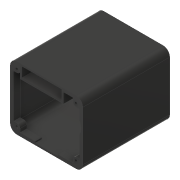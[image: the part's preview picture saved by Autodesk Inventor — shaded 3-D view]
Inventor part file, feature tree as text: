
AUTODESK INVENTOR PART (.ipt)
format: ipt  version: 2017 (Build 210142000, 142)  size: 1,119,232 bytes
history: native  units: in
note: dims shown in document units (in); Inventor stores cm internally (conversion verified against a paired STEP export)
features: sketch x38, extrude x36, projected_geometry x25, reference x20, other x11, fillet x4, chamfer x3, plane x3
ambient origin geometry x8: Origin, YZ Plane, XZ Plane, XY Plane, X Axis, Y Axis, Z Axis, Center Point
bodies: Solid1 (feature_tree)
feature tree (140):
  extrude  "Extrusion1"  Depth=3.25in
  extrude  "Extrusion2"  Depth=0.125in TaperAngle=0.0deg
  extrude  "Extrusion3"  Depth=0.125in
  chamfer  "Chamfer1"  Distance=0.125in
  sketch  "Sketch4"  dims[d8=0.125in]
  plane  "Work Plane1"
  extrude  "Extrusion4"  Depth=0.25in
  chamfer  "Chamfer2"  Distance=0.25in
  extrude  "Extrusion5"  Depth=0.1in
  extrude  "Extrusion6"  Depth=0.1in
  extrude  "Extrusion7"  Depth=0.1in
  fillet  "Fillet1"  Radius=0.275in
  extrude  "Extrusion8"  Depth=0.0625in TaperAngle=0.0deg
  fillet  "Fillet2"  Radius=0.0625in
  fillet  "Fillet3"  Radius=0.0625in
  extrude  "Extrusion9"  Depth=0.05in
  extrude  "Extrusion10"  Depth=0.05in
  fillet  "Fillet4"  Radius=2.5in
  sketch  "Sketch13"  dims[d30=0.175in d31=0.0in d32=1.0in d33=0.0in d34=0.0625in d35=0.0625in]
  plane  "Work Plane2"
  extrude  "Extrusion11"  Depth=0.125in TaperAngle=0.0deg
  sketch  "Sketch14"  dims[d36=0.0625in d37=0.05in]
  plane  "Work Plane3"
  extrude  "Extrusion12"  Depth=0.05in
  extrude  "Extrusion13"  Depth=0.25in
  extrude  "Extrusion14"  Depth=0.05in
  extrude  "Extrusion16"  Depth=0.05in
  extrude  "Extrusion17"  [1 undecoded]
  extrude  "Extrusion18"  Depth=0.0625in TaperAngle=0.0deg
  extrude  "Extrusion19"  Depth=0.5in TaperAngle=0.0deg
  sketch  "Sketch24"  dims[d58=0.25in d59=0.0in d60=0.0625in d61=0.0in]
  extrude  "Extrusion20"  Depth=0.01in
  extrude  "Extrusion21"  TaperAngle=0.0deg  [1 undecoded]
  extrude  "Extrusion22"  Depth=1.0in TaperAngle=0.0deg
  extrude  "Extrusion23"  Depth=0.85in
  extrude  "Extrusion24"  Depth=0.0625in
  extrude  "Extrusion25"  Depth=0.375in
  extrude  "Extrusion26"  Depth=0.1in
  extrude  "Extrusion27"  Depth=0.25in TaperAngle=0.0deg
  extrude  "Extrusion28"  Depth=0.0625in
  extrude  "Extrusion29"  Depth=0.25in TaperAngle=0.0deg
  extrude  "Extrusion30"  Depth=0.1in
  extrude  "Extrusion31"  Depth=0.1in TaperAngle=0.0deg
  extrude  "Extrusion32"  Depth=0.1in TaperAngle=0.0deg
  extrude  "Extrusion33"  Depth=0.375in
  extrude  "Extrusion34"  Depth=0.125in TaperAngle=45.0deg
  chamfer  "Chamfer3"  Distance=0.1in
  extrude  "Extrusion35"  Depth=0.1in TaperAngle=0.0deg
  extrude  "Extrusion36"  [1 undecoded]
  extrude  "Extrusion37"  [1 undecoded]
  sketch  "Sketch1"  dims[d0=3.25in d1=0.0in d2=0.015in]
  reference  "Reference1"
  sketch  "Sketch2"  dims[d3=0.015in d4=0.125in d5=0.0in]
  reference  "Reference2"
  reference  "Reference3"
  reference  "Reference4"
  reference  "Reference5"
  reference  "Reference6"
  sketch  "Sketch3"  dims[d6=0.125in d7=0.125in]
  projected_geometry  "Projected Loop1"
  projected_geometry  "Projected Loop2"
  reference  "Reference7"
  reference  "Reference8"
  reference  "Reference9"
  reference  "Reference10"
  reference  "Reference11"
  sketch  "Sketch5"  dims[d9=0.125in d10=0.125in d11=0.0in]
  reference  "Reference12"
  reference  "Reference13"
  sketch  "Sketch6"  dims[d12=0.057in d13=0.125in d14=45.0deg d15=0.25in]
  sketch  "Sketch8"  dims[d16=0.1in]
  projected_geometry  "Projected Loop3"
  sketch  "Sketch9"  dims[d17=0.1in d19=0.25in d20=0.0in]
  reference  "Reference14"
  reference  "Reference15"
  sketch  "Sketch10"  dims[d21=0.075in d22=0.125in d23=45.0deg d24=0.1in]
  projected_geometry  "Projected Loop4"
  projected_geometry  "Projected Loop5"
  sketch  "Sketch11"  dims[d25=0.5in d26=0.1in]
  projected_geometry  "Projected Loop6"
  sketch  "Sketch12"  dims[d27=0.1in d28=0.275in d29=0.275in]
  projected_geometry  "Projected Loop7"
  projected_geometry  "Projected Loop8"
  projected_geometry  "Projected Loop9"
  sketch  "Sketch15"  dims[d38=0.05in d39=0.05in d40=2.5in d41=0.0in]
  projected_geometry  "Projected Loop10"
  projected_geometry  "Projected Loop11"
  sketch  "Sketch17"  dims[d42=0.125in d43=2.5in d44=0.0in]
  projected_geometry  "Projected Loop25"
  sketch  "Sketch18"  dims[d45=0.125in d46=0.05in]
  projected_geometry  "Projected Loop26"
  projected_geometry  "Projected Loop27"
  sketch  "Sketch20"  dims[d47=0.0625in d48=0.0in d49=0.25in]
  reference  "Reference18"
  projected_geometry  "Projected Loop28"
  sketch  "Sketch21"  dims[d50=0.1in d51=0.05in]
  projected_geometry  "Projected Loop29"
  sketch  "Sketch22"  dims[d52=0.0625in d53=0.0in d54=0.05in]
  sketch  "Sketch23"  dims[d55=0.0625in d56=0.0in d57=-0.25in]
  projected_geometry  "Projected Loop30"
  projected_geometry  "Projected Loop31"
  projected_geometry  "Projected Loop32"
  sketch  "Sketch25"  dims[d62=0.0625in d63=0.0in d66=0.5in d67=0.0in]
  sketch  "Sketch26"  dims[d69=0.01in d70=0.01in]
  sketch  "Sketch27"  dims[d71=0.5in d72=0.0in d73=0.0in d74=0.0in]
  sketch  "Sketch28"  dims[d75=1.0in d76=0.0in d77=1.0in d78=0.0in]
  sketch  "Sketch29"  dims[d79=0.25in d80=0.0in d81=0.85in]
  projected_geometry  "Projected Loop33"
  projected_geometry  "Projected Loop34"
  sketch  "Sketch30"  dims[d82=0.25in d83=0.0in d85=0.0625in]
  reference  "Reference19"
  sketch  "Sketch31"  dims[d86=0.0625in d88=0.375in]
  reference  "Reference20"
  sketch  "Sketch32"  dims[d89=2.625in d90=0.0in d91=0.1in]
  projected_geometry  "Projected Loop35"
  projected_geometry  "Projected Loop36"
  sketch  "Sketch33"  dims[d92=0.25in d93=0.0in d94=0.25in d95=0.0in]
  reference  "Reference21"
  reference  "Reference22"
  sketch  "Sketch34"  dims[d96=1.5in d97=0.0625in]
  projected_geometry  "Projected Loop37"
  sketch  "Sketch35"  dims[d98=0.25in d99=0.0in d100=1.0in d101=0.0in]
  sketch  "Sketch36"  dims[d102=0.1in d103=0.0in d104=0.1in]
  projected_geometry  "Projected Loop38"
  sketch  "Sketch37"  dims[d105=0.1in d106=0.0in d107=0.1in d108=0.0in]
  sketch  "Sketch38"  dims[d109=0.1in d110=0.0in d111=0.1in d112=0.0in]
  sketch  "Sketch39"  dims[d113=0.1in d114=0.0in d115=0.375in]
  sketch  "Sketch40"  dims[d116=0.1in d117=0.0in d118=0.125in d119=0.125in d120=45.0deg d121=0.1in d122=0.0in]
  sketch  "Sketch41"  dims[d123=0.1in d124=0.0in d125=0.1in d126=0.0in]
  parser-record x1  (decoder bookkeeping rows leaked as tree rows — omitted from the tree; the rows remain in map.json)
  other  "Assembly1.iam"
  other  "Faceplate:1"
  other  "Cap Top Cap:1"
  other  "Holder:1"
  other  "battery:2"
  other  "battery:1"
  other  "Assembly with Fan.iam"
  other  "Bottom Assembly:1"
  other  "Bottom:1"
  other  "Small Heater Holder for Use With Fan:1"
note: 4 required parameter values undecoded (feature->parameter linkage not recoverable at this tier; creation-order binding heuristic only, values carry confidence <= 0.55)
note: 1 file-system path scrubbed to <path> (originals preserved in map.json)
